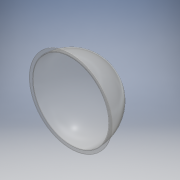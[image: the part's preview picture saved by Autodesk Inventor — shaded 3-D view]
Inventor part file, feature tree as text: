
AUTODESK INVENTOR PART (.ipt)
format: ipt  version: 2016 (Build 200138000, 138)  size: 177,664 bytes
history: native  units: mm
features: fillet x2, sketch x2, revolve x1, extrude x1
ambient origin geometry x8: Origin, YZ Plane, XZ Plane, XY Plane, X Axis, Y Axis, Z Axis, Center Point
bodies: Solid1 (feature_tree)
feature tree (6):
  revolve  "Revolution1"  [1 undecoded]
  extrude  "Extrusion1"  Depth=2.0mm
  fillet  "Fillet1"  Radius=4.0mm
  fillet  "Fillet2"  Radius=2.0mm
  sketch  "Sketch1"  dims[d0=590.0mm d1=598.0mm]
  sketch  "Sketch2"  dims[d2=180.0deg d3=645.0mm d4=4.0mm d5=0.0mm d6=2.0mm d7=2.0mm]
note: 1 required parameter value undecoded (feature->parameter linkage not recoverable at this tier; creation-order binding heuristic only, values carry confidence <= 0.55)
